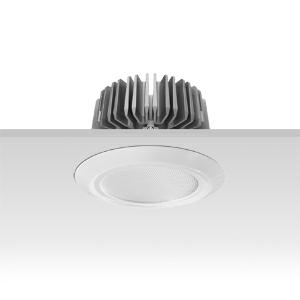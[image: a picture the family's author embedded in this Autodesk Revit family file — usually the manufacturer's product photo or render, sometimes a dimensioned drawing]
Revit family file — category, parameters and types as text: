
# Revit family: 3f_filippi_-_3f_reno_bianco_ampio_3f_filippi_-_30387_a01046_-_3f_reno_150_wh_3000-930_dali_wide___smp_wh_d388
name_source: partatom
category: Lighting Fixtures
units: mm (PartAtom-declared; Revit-internal decimal feet)

## family parameters
Cut with Voids When Loaded = No
Host = Face
Light Source = No
Part Type = Normal
Room Calculation Point = No
Round Connector Dimension = Use Diameter
Shared = No

## types (1)
- 3F Filippi - 3F Reno Bianco Ampio (1 x LED, 2324 lm, 37 W, 3000 K)
    Apparent Load = 37 VA
    Approval mark = CE
    CIE Flux Codes = 73 92 98 100 100
    Color Rendering = 90
    Color Temperature = 3000 K
    Control Gear = Electronic transformer
    Default Elevation = 1800 mm
    Description = ILLUMINOTECHNICAL
Luminous efficiency 100% (DLOR 100%, ULOR 0%).
Initial luminous flux of the luminaire 2324 lm.
Direct symmetric wide distribution.
Installation Interdistance Transv.D = 1.01 x hu - Long.D = 1.00 x hu.
Tabular UGR (CIE 117 - 4H-8H; S=0.25H; 70/50/20): RUG 24.5 - 24.5.
Beam angle: 70° - 70°.
Luminous efficacy 63 lm/W.
Lifetime (L90/B10): 30000 h. (tq+25°C)
Lifetime (L85/B10): 50000 h. (tq+25°C)
Lifetime (L70/B10): 80000 h. (tq+25°C)
Sudden decreased luminous flux after 50000 hours: 0% (C0).
Photobiological safety in compliance with IEC/TR 62778: RG0 risk exempt, (IEC 62471).
In compliance with IEC/EN 62722-2-1 - IEC/EN 62717 standards.

SOURCE
Compact LED module 3000/930.
Energy efficiency class (UE 2019/2020 - UE 2019/2015): F.
CIE 13.3 Colour rendering index: CRI >90 (R9 >50%).
IES TM-30 Fidelity Index: Rf = 92 Rg = 101.
CCT nominal colour temperature 3000 K.
Colour initial tolerance (MacAdam): SDCM 3.
Zhaga Book 3 compliant.

MECHANICAL
Passive heat dissipator in die-casting aluminium, oversized, for optimum thermal management of the LED module.
Parabolic element with graduated/concentric rings in white polycarbonate.
Transparent external lens with glossy and satin differentiated surfaces, with a cooling and anti-insect system in methacrylate (PMMA).
Fastening spring clips in stainless steel.
Dimensions: diameter 176 mm, height 111 mm. Weight 1.45 kg.
IP44 protection degree for exposed part, IP20 for recessed part.
Mechanical strength to impacts IK05 (0.7 joule).
Glow-wire test resistance 650°C.

ELECTRICAL
Wiring on a separate unit.
Halogen Free DALI-2 DATI (Parts 251, 252, 253), PUSH-DIM, electronic wiring 230V-50/60Hz, power factor 0.97 at full load, THD <25%, constant output current, SELV, class II, 1 driver, 1 DALI addresse.
Power of the luminaire 37 W.
ENEC - CE.
SAFE FLICKER: PstLM=<1 and SVM=<0.4 (IEC TR 61547-1 and IEC TR 63158), to ensure a more comfortable and safe light.
Luminaire compliant with EN 60598-2-22 for power supply from a centralised emergency system CPSS (Central Power Supply System), not incorporated in the luminaire - high risk areas excluded. The default power and flux are 100% in AC and 100% in DC.
Ambient temperature from 0°C to +25°C.
Temperature class T6 max 85°C.
Relative humidity UR: <85%.

INSTALLATION
Pull-up recessed fitting.
False ceiling carving: 150 mm.
All accessories dedicated to this product are available on the Catalog and on our website www.3F-Filippi.com.

ACCESSORIES
A01046 - Anti-glare microprismatic SMP diffuser in methacrylate (PMMA), locked and in line with the trim, in white polycarbonate.

APPLICATIONS
Suitable product for food production plants (HACCP), IFS (Food Version 6), BRC (GSFS Food Version 7).
Environments: architectural, commercial, exhibition areas, transit areas, corridors, shops, display windows, service areas.
In false ceilings with narrow voids.

LIGHT MANAGEMENT
Recommended minimum setting: 10%.
The luminaire, equipped with (DALI-2 DATI) driver, can be controlled manually with 3F Easy Dim technology or automatically/manually with wired or wireless DALI/D2D control systems.
The D2D driver guarantees interoperability with other devices with the same certification by making the following information available:
Device Data (Part 251), Energy Report (Part 252), Diagnosis & Maintenance (Part 253).
In electrical systems without a regulation system (manual or automatic) and DALI bus, a suitable jumper must be made on the DA-DA terminals of the appliance.

WARNING
Luminaire designed for disposal/recycling at end-of-life.
Replaceable (LED only) light source by a professional. Replaceable control gear by a professional.
    Height = 0 mm  [stored 0 ft]
    Lamp = 1 x LED
    Lamp Light Flux = 2324 lm
    Lamp Power = 37 W
    Lamp count = 1
    Length = 176 mm
    Lifetime = 50000 h
    Luminous efficacy = 63 lm/W
    Manufacturer = 3F Filippi
    ModVariant = No
    Model = 3F Filippi - 30387+A01046 - 3F Reno 150 WH 3000-930 DALI WIDE + SMP WH
    Mounting Place = Ceiling
    Mounting Type = Recessed
    Number of Poles = 1
    OnlyDefault = Yes
    Power Factor = 1
    Product Name = 3F Filippi - 3F Reno Bianco Ampio
    Product group = recessed luminaire
    ProductGroupID = 4
    Protection Class = Protection class II
    Protection Degree = IP 20
    RLX_Detail_Level = 1
    RLX_Emergency_Light_Flux = 0 lm
    RLX_Emergency_Type = 0
    RLX_Emergency_Type_DB = No
    RlxData = <blob elided: 85825 chars, md5=c9d7c61c>
    Socket = socket
    Standby Power = 0 W
    System Light Flux = 2324 lm
    System Power = 37 W
    Type Comments = Product without accessories
    Type Image = 3ffilippi_3f_reno_150_wh_vs_smp.jpg
    URL = http://relux.com
    VarID = ---
    Voltage = 0 V
    Weight = 0.00 kg
    Width = 0 mm  [stored 0 ft]

note: [stored X ft] marks values corroborated as IEEE doubles in the binary element streams (Revit-internal decimal feet)

## geometry (parser evidence)
native form markers: Blend x4, Sweep x11
no freeform markers — native parametric forms only
